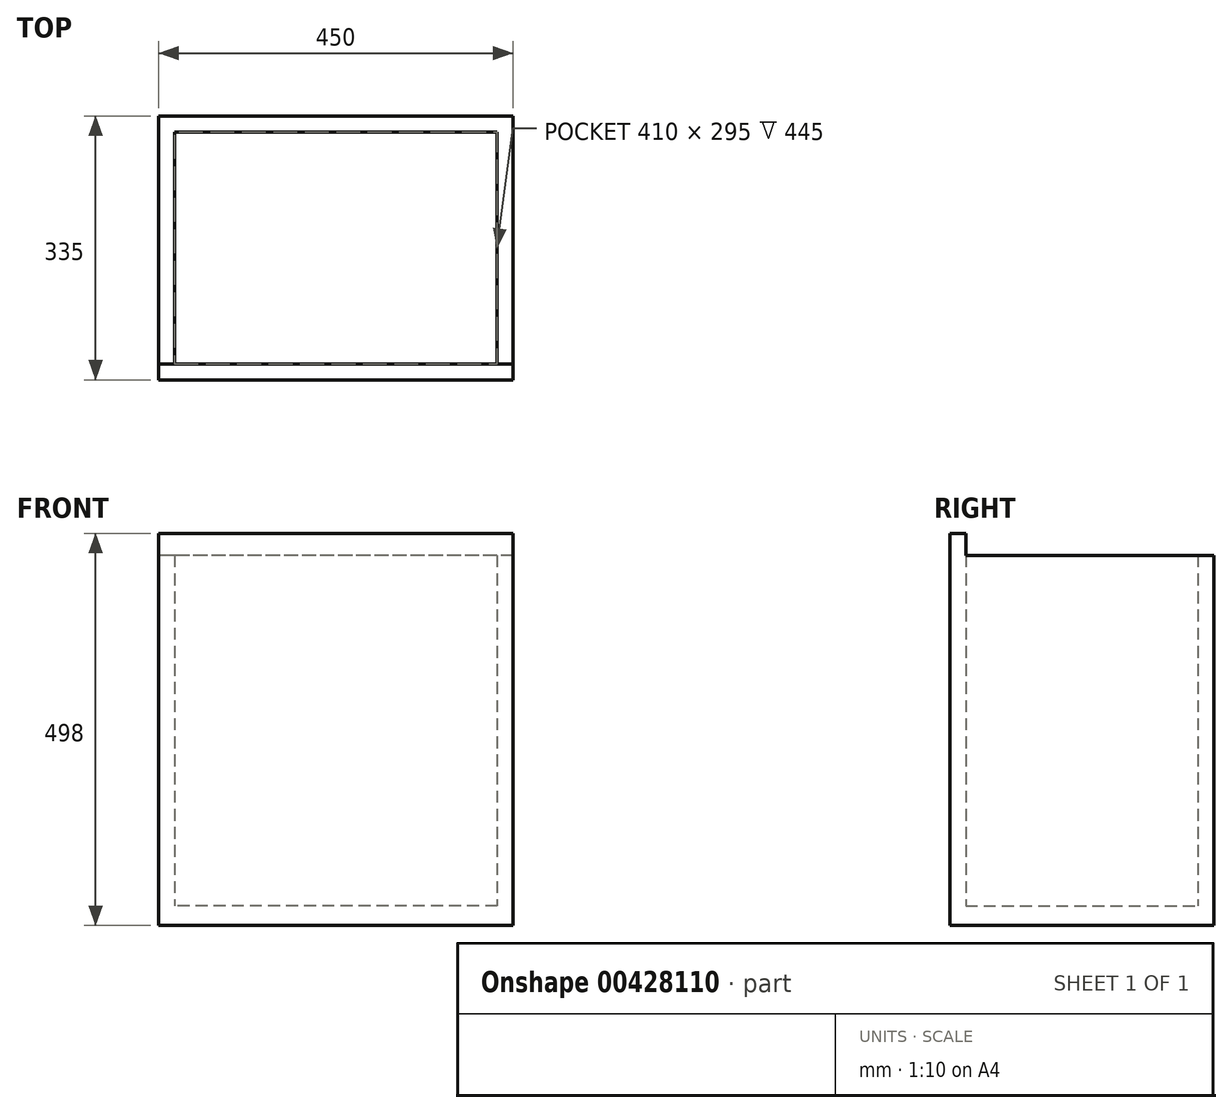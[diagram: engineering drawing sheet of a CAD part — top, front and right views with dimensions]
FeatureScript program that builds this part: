
annotation { "Feature Type Name" : "Feature", "Feature Type Description" : "" }
export const myFeature = defineFeature(function(context is Context, id is Id, definition is map)
    precondition{}
    {
        {
            var Q0;
            Q0=qCreatedBy(makeId("Top.planeOp"),FACE);
            var sketch = newSketch(context, id + "F0", { "sketchPlane" : qUnion([Q0])});
            skLineSegment(sketch, "E0.bottom", {"start": v(225, -167.5) * mm, "end": v(-225, -167.5) * mm});
            skLineSegment(sketch, "E0.top", {"start": v(225, 167.5) * mm, "end": v(-225, 167.5) * mm});
            skLineSegment(sketch, "E0.left", {"start": v(225, -167.5) * mm, "end": v(225, 167.5) * mm});
            skLineSegment(sketch, "E0.right", {"start": v(-225, -167.5) * mm, "end": v(-225, 167.5) * mm});
            skPoint(sketch, "E0.middle", {"position": v(0, 0) * mm});
            skLineSegment(sketch, "E1.0", {"start": v(205, -167.5) * mm, "end": v(205, 167.5) * mm});
            skLineSegment(sketch, "E2.0", {"start": v(225, 147.5) * mm, "end": v(-225, 147.5) * mm});
            skLineSegment(sketch, "E3.0", {"start": v(-205, -167.5) * mm, "end": v(-205, 167.5) * mm});
            skLineSegment(sketch, "E4.0", {"start": v(225, -147.5) * mm, "end": v(-225, -147.5) * mm});
            skSolve(sketch);
        }
        {
            var Q0;
            {var subQ0=sQuery(id+"F0.wireOp",EDGE,"E1.0");var subQ1=sQuery(id+"F0.wireOp",EDGE,"E0.bottom");var subQ2=makeQuery(id+"F0.imprint","INTERSECT",VERTEX,{"derivedFrom":[subQ1,subQ0]});Q0=makeQuery(id+"F0.imprint","IMPRINT",FACE,{"disambiguationData":[TD([[makeQuery(id+"F0.imprint","IMPRINT",EDGE,{"disambiguationData":[TD([[subQ2,-1.0]])],"derivedFrom":subQ1}),-1.0]])]});}
            var Q1;
            {var subQ0=sQuery(id+"F0.wireOp",EDGE,"E0.right");var subQ1=sQuery(id+"F0.wireOp",EDGE,"E0.bottom");var subQ2=makeQuery(id+"F0.imprint","INTERSECT",VERTEX,{"derivedFrom":[subQ1,subQ0]});Q1=makeQuery(id+"F0.imprint","IMPRINT",FACE,{"disambiguationData":[TD([[makeQuery(id+"F0.imprint","IMPRINT",EDGE,{"disambiguationData":[TD([[subQ2,1.0]])],"derivedFrom":subQ1}),-1.0]])]});}
            var Q2;
            {var subQ0=sQuery(id+"F0.wireOp",EDGE,"E0.left");var subQ1=sQuery(id+"F0.wireOp",EDGE,"E0.bottom");var subQ2=makeQuery(id+"F0.imprint","INTERSECT",VERTEX,{"derivedFrom":[subQ1,subQ0]});Q2=makeQuery(id+"F0.imprint","IMPRINT",FACE,{"disambiguationData":[TD([[makeQuery(id+"F0.imprint","IMPRINT",EDGE,{"disambiguationData":[TD([[subQ2,-1.0]])],"derivedFrom":subQ1}),-1.0]])]});}
            extrude(context, id + "F1", {"entities" : qUnion([Q0, Q1, Q2]), "depth" : 498 * mm});
        }
        {
            var Q0;
            {var subQ0=sQuery(id+"F0.wireOp",EDGE,"E2.0");var subQ1=sQuery(id+"F0.wireOp",EDGE,"E0.right");var subQ2=makeQuery(id+"F0.imprint","INTERSECT",VERTEX,{"derivedFrom":[subQ1,subQ0]});Q0=makeQuery(id+"F0.imprint","IMPRINT",FACE,{"disambiguationData":[TD([[makeQuery(id+"F0.imprint","IMPRINT",EDGE,{"disambiguationData":[TD([[subQ2,1.0]])],"derivedFrom":subQ1}),-1.0]])]});}
            var Q1;
            {var subQ0=sQuery(id+"F0.wireOp",EDGE,"E0.right");var subQ1=sQuery(id+"F0.wireOp",EDGE,"E0.top");var subQ2=makeQuery(id+"F0.imprint","INTERSECT",VERTEX,{"derivedFrom":[subQ1,subQ0]});Q1=makeQuery(id+"F0.imprint","IMPRINT",FACE,{"disambiguationData":[TD([[makeQuery(id+"F0.imprint","IMPRINT",EDGE,{"disambiguationData":[TD([[subQ2,1.0]])],"derivedFrom":subQ1}),1.0]])]});}
            var Q2;
            {var subQ0=sQuery(id+"F0.wireOp",EDGE,"E1.0");var subQ1=sQuery(id+"F0.wireOp",EDGE,"E0.top");var subQ2=makeQuery(id+"F0.imprint","INTERSECT",VERTEX,{"derivedFrom":[subQ1,subQ0]});Q2=makeQuery(id+"F0.imprint","IMPRINT",FACE,{"disambiguationData":[TD([[makeQuery(id+"F0.imprint","IMPRINT",EDGE,{"disambiguationData":[TD([[subQ2,-1.0]])],"derivedFrom":subQ1}),1.0]])]});}
            var Q3;
            {var subQ0=sQuery(id+"F0.wireOp",EDGE,"E0.left");var subQ1=sQuery(id+"F0.wireOp",EDGE,"E0.top");var subQ2=makeQuery(id+"F0.imprint","INTERSECT",VERTEX,{"derivedFrom":[subQ1,subQ0]});Q3=makeQuery(id+"F0.imprint","IMPRINT",FACE,{"disambiguationData":[TD([[makeQuery(id+"F0.imprint","IMPRINT",EDGE,{"disambiguationData":[TD([[subQ2,-1.0]])],"derivedFrom":subQ1}),1.0]])]});}
            var Q4;
            {var subQ0=sQuery(id+"F0.wireOp",EDGE,"E2.0");var subQ1=sQuery(id+"F0.wireOp",EDGE,"E0.left");var subQ2=makeQuery(id+"F0.imprint","INTERSECT",VERTEX,{"derivedFrom":[subQ1,subQ0]});Q4=makeQuery(id+"F0.imprint","IMPRINT",FACE,{"disambiguationData":[TD([[makeQuery(id+"F0.imprint","IMPRINT",EDGE,{"disambiguationData":[TD([[subQ2,1.0]])],"derivedFrom":subQ1}),1.0]])]});}
            extrude(context, id + "F2", {"entities" : qUnion([Q0, Q1, Q2, Q3, Q4]), "operationType" : NewBodyOperationType.ADD, "depth" : 470 * mm});
        }
        {
            var Q0;
            Q0 = qSketchRegion(id + "F0", true);
            var Q1;
            {var subQ0=sQuery(id+"F0.wireOp",EDGE,"E4.0");var subQ1=sQuery(id+"F0.wireOp",EDGE,"E1.0");var subQ2=makeQuery(id+"F0.imprint","INTERSECT",VERTEX,{"derivedFrom":[subQ1,subQ0]});Q1=makeQuery(id+"F0.imprint","IMPRINT",FACE,{"disambiguationData":[TD([[makeQuery(id+"F0.imprint","IMPRINT",EDGE,{"disambiguationData":[TD([[subQ2,-1.0]])],"derivedFrom":subQ1}),1.0]])]});}
            extrude(context, id + "F3", {"entities" : qUnion([Q0, Q1]), "operationType" : NewBodyOperationType.ADD, "depth" : 25 * mm});
        }
    });
